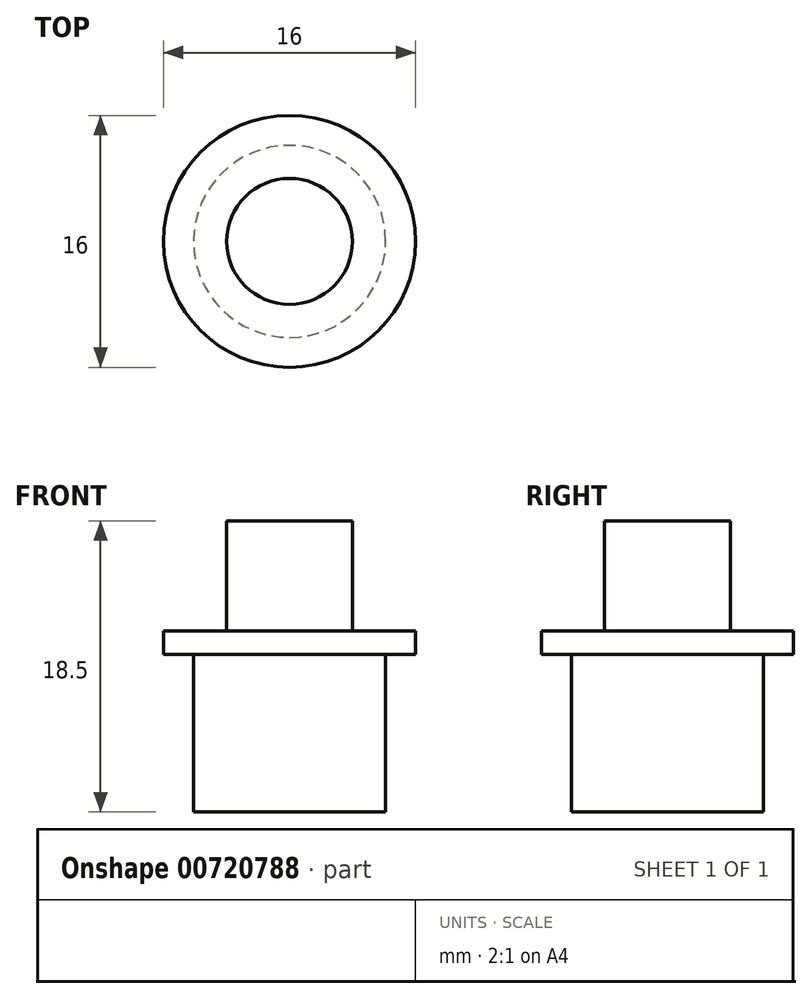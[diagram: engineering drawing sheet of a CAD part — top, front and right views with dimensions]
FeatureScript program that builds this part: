
annotation { "Feature Type Name" : "Feature", "Feature Type Description" : "" }
export const myFeature = defineFeature(function(context is Context, id is Id, definition is map)
    precondition{}
    {
        {
            var Q0;
            Q0=qCreatedBy(makeId("Top.planeOp"),FACE);
            var sketch = newSketch(context, id + "F0", { "sketchPlane" : qUnion([Q0])});
            skCircle(sketch, "E0", {"center": v(0, 0) * mm, "radius": 6.1 * mm});
            skCircle(sketch, "E1", {"center": v(0, 0) * mm, "radius": 4 * mm});
            skSolve(sketch);
        }
        {
            var Q0;
            Q0 = qSketchRegion(id + "F0", true);
            extrude(context, id + "F1", {"entities" : qUnion([Q0]), "depth" : 10 * mm, "offsetDistance" : 25 * mm});
        }
        {
            var Q0;
            Q0=makeQuery(id+"F0.imprint","IMPRINT",FACE,{"disambiguationData":[TD([[makeQuery(id+"F0.imprint","IMPRINT",EDGE,{"derivedFrom":sQuery(id+"F0.wireOp",EDGE,"E1")}),1.0]])]});
            extrude(context, id + "F2", {"entities" : qUnion([Q0]), "operationType" : NewBodyOperationType.ADD, "depth" : 18.5 * mm, "offsetDistance" : 25 * mm});
        }
        {
            var Q0;
            Q0=makeQuery(id+"F1.opExtrude","CAP_FACE",FACE,{"disambiguationData":[OSD([sQuery(id+"F0.wireOp",EDGE,"E0"),sQuery(id+"F0.wireOp",EDGE,"E1")])],"isStart":false});
            var sketch = newSketch(context, id + "F3", { "sketchPlane" : qUnion([Q0])});
            skCircle(sketch, "E2", {"center": v(0, 0) * mm, "radius": 8 * mm});
            skSolve(sketch);
        }
        {
            var Q0;
            Q0 = qSketchRegion(id + "F3", true);
            extrude(context, id + "F4", {"entities" : qUnion([Q0]), "operationType" : NewBodyOperationType.ADD, "depth" : 1.5 * mm, "offsetDistance" : 25 * mm});
        }
    });
